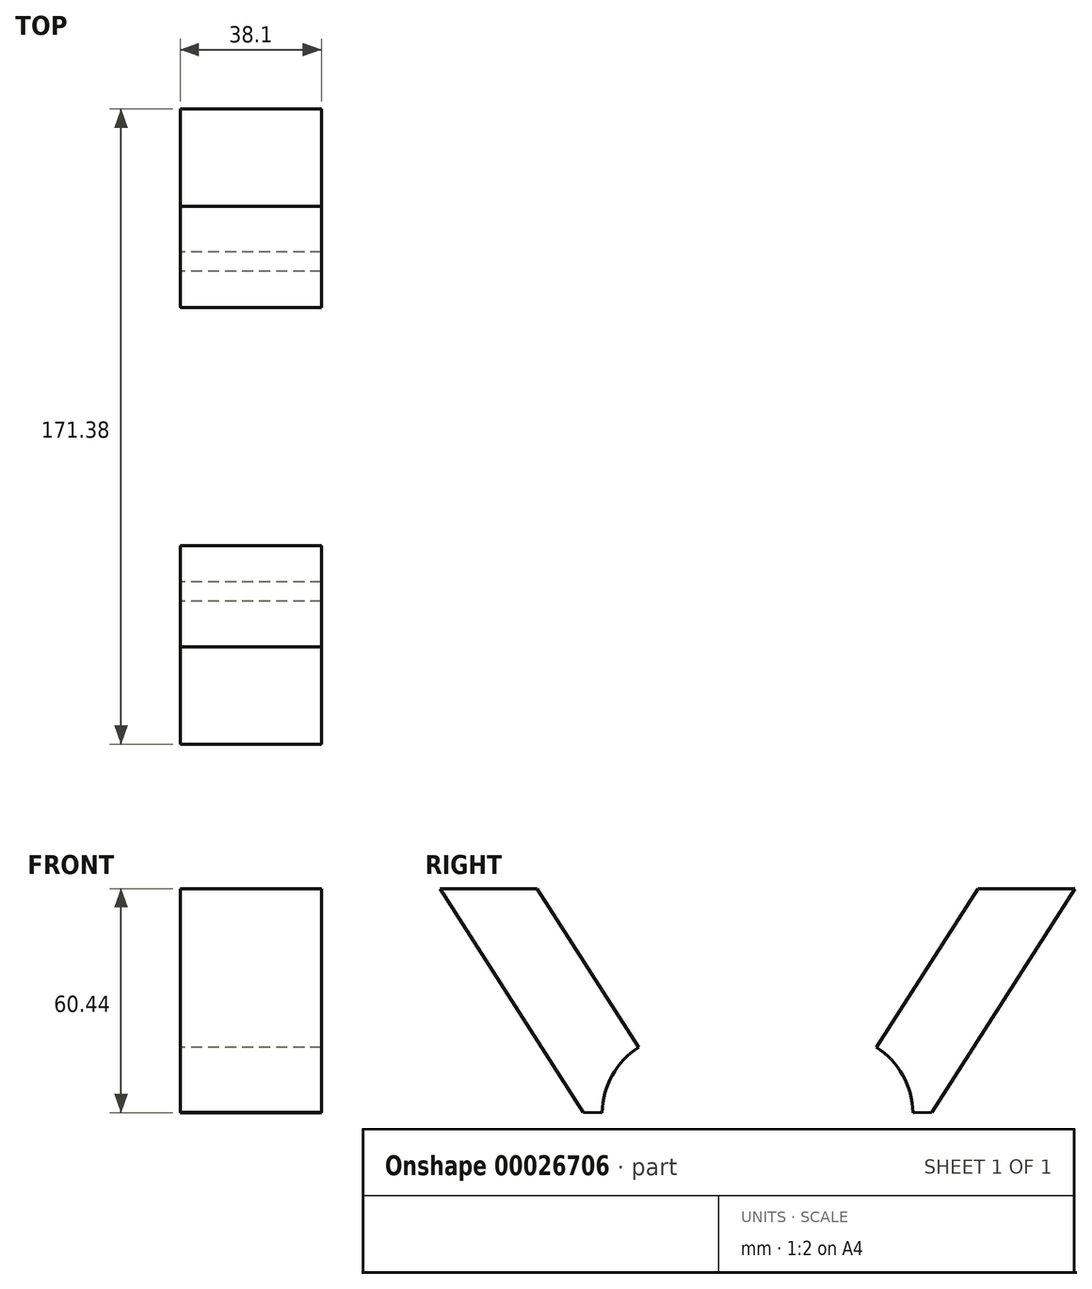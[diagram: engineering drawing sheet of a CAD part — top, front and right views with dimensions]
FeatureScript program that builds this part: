
annotation { "Feature Type Name" : "Feature", "Feature Type Description" : "" }
export const myFeature = defineFeature(function(context is Context, id is Id, definition is map)
    precondition{}
    {
        {
            var Q0;
            Q0=qCreatedBy(makeId("Right.planeOp"),FACE);
            var sketch = newSketch(context, id + "F0", { "sketchPlane" : qUnion([Q0])});
            skLineSegment(sketch, "E0", {"start": v(-47.08, 5.81) * mm, "end": v(-85.7, 66.17) * mm});
            skLineSegment(sketch, "E1", {"start": v(-85.7, 66.17) * mm, "end": v(-59.47, 66.17) * mm});
            skLineSegment(sketch, "E2", {"start": v(-59.47, 66.17) * mm, "end": v(-32.1, 23.37) * mm});
            skLineSegment(sketch, "E3", {"start": v(-41.93, 5.73) * mm, "end": v(-47.08, 5.81) * mm});
            skArc(sketch, "E4", {"start": v(-32.1, 23.37) * mm, "mid": v(-39.23, 15.79) * mm, "end": v(-41.93, 5.73) * mm});
            skSolve(sketch);
        }
        {
            var Q0;
            Q0 = qSketchRegion(id + "F0", true);
            extrude(context, id + "F1", {"entities" : qUnion([Q0]), "depth" : 38.1 * mm});
        }
        {
            var Q0;
            Q0=makeQuery(id+"F1.opExtrude","SWEPT_BODY",BODY,{"disambiguationData":[OSD([sQuery(id+"F0.wireOp",EDGE,"E0"),sQuery(id+"F0.wireOp",EDGE,"E1"),sQuery(id+"F0.wireOp",EDGE,"E2"),sQuery(id+"F0.wireOp",EDGE,"E3"),sQuery(id+"F0.wireOp",EDGE,"E4")])]});
            var Q1;
            Q1=qCreatedBy(makeId("Front.planeOp"),FACE);
            mirror(context, id + "F2", {"entities" : qUnion([Q0]), "mirrorPlane" : qUnion([Q1])});
        }
    });
